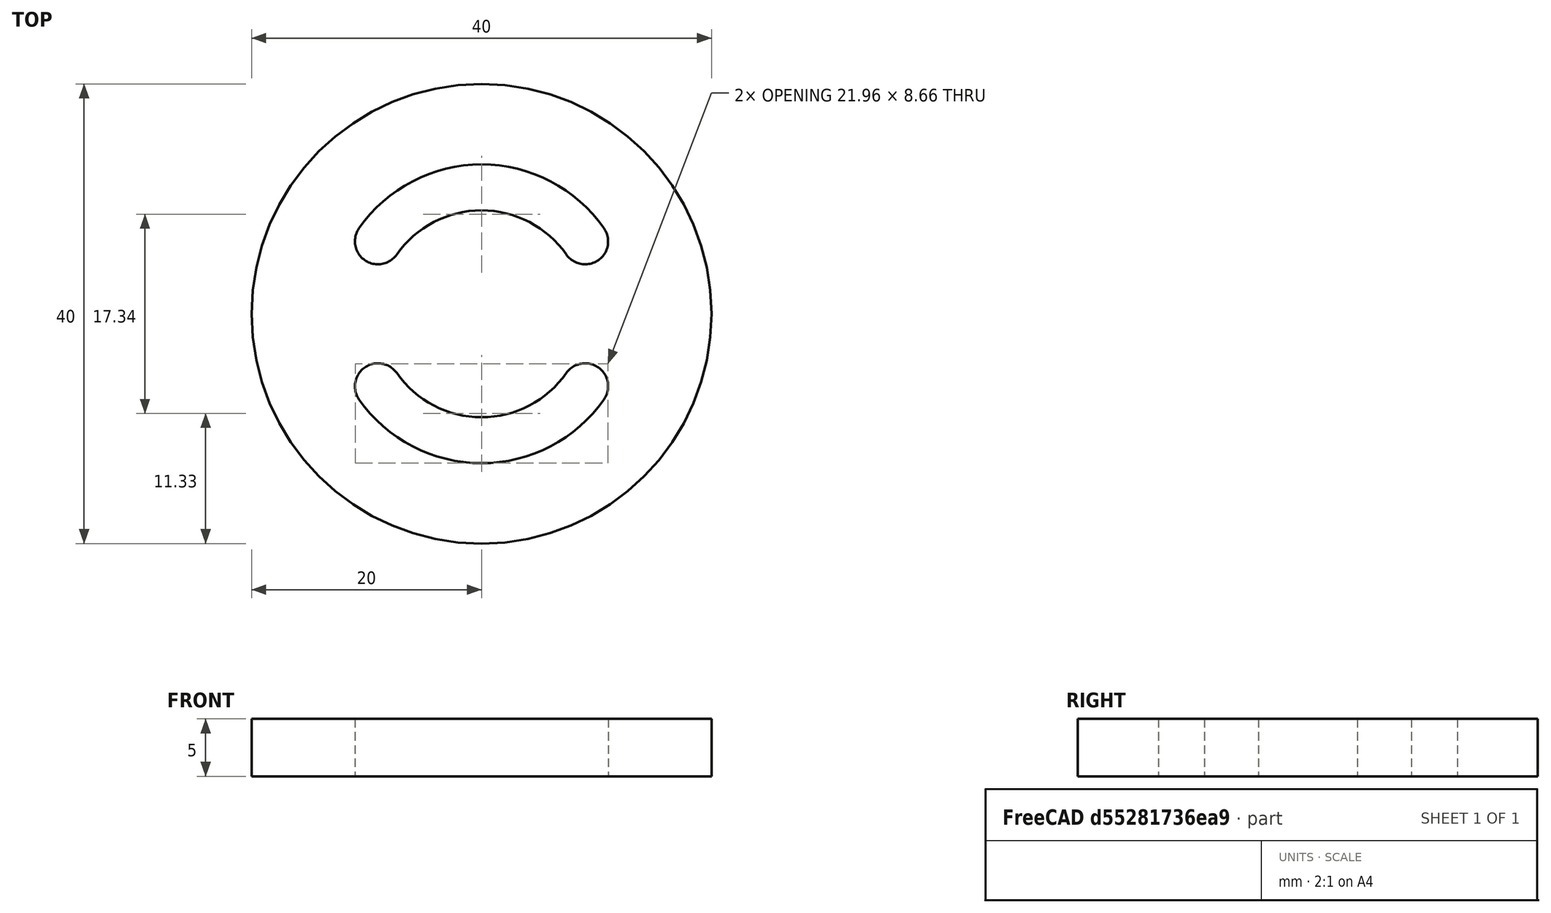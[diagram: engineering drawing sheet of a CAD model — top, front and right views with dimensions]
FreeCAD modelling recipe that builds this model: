
FCSTD DOCUMENT  (FreeCAD 0.16RUnknown)
Label: joint-i
License: All rights reserved
LicenseURL: http://en.wikipedia.org/wiki/All_rights_reserved
objects: Sketcher::SketchObject×1, Part::Extrusion×1
note: 2 computed .brp shape members not serialized (recipe doc carries the construction recipe); baked Part::Feature solids carry a one-line shape summary decoded from their .brp

FEATURE [Sketcher::SketchObject] Sketch
  sketch-geometry (23):
    g0: Circle CenterX=0 CenterY=0 CenterZ=0 NormalX=0 NormalY=0 NormalZ=1 Radius=20
    g1: ArcOfCircle [constr] CenterX=0 CenterY=0 CenterZ=0 NormalX=0 NormalY=0 NormalZ=1 Radius=13 StartAngle=2.53073 EndAngle=3.75246
    g2: ArcOfCircle [constr] CenterX=0 CenterY=0 CenterZ=0 NormalX=0 NormalY=0 NormalZ=1 Radius=9 StartAngle=2.53073 EndAngle=3.75246
    g3: ArcOfCircle [constr] CenterX=0 CenterY=0 CenterZ=0 NormalX=0 NormalY=0 NormalZ=1 Radius=9 StartAngle=5.67232 EndAngle=6.89405
    g4: ArcOfCircle [constr] CenterX=0 CenterY=0 CenterZ=0 NormalX=0 NormalY=0 NormalZ=1 Radius=13 StartAngle=5.67232 EndAngle=6.89405
    g5: ArcOfCircle CenterX=0 CenterY=0 CenterZ=0 NormalX=0 NormalY=0 NormalZ=1 Radius=9 StartAngle=0.610865 EndAngle=2.53073
    g6: ArcOfCircle CenterX=0 CenterY=0 CenterZ=0 NormalX=0 NormalY=0 NormalZ=1 Radius=13 StartAngle=0.610865 EndAngle=2.53073
    g7: ArcOfCircle CenterX=0 CenterY=0 CenterZ=0 NormalX=0 NormalY=0 NormalZ=1 Radius=9 StartAngle=3.75246 EndAngle=5.67232
    g8: ArcOfCircle CenterX=0 CenterY=0 CenterZ=0 NormalX=0 NormalY=0 NormalZ=1 Radius=13 StartAngle=3.75246 EndAngle=5.67232
    g9: LineSegment [constr] StartX=-10.649 StartY=7.45649 StartZ=0 EndX=-7.37237 EndY=5.16219 EndZ=0
    g10: LineSegment [constr] StartX=-7.37237 StartY=5.16219 StartZ=0 EndX=0 EndY=0 EndZ=0
    g11: LineSegment [constr] StartX=0 StartY=0 StartZ=0 EndX=7.37237 EndY=-5.16219 EndZ=0
    g12: LineSegment [constr] StartX=7.37237 StartY=-5.16219 StartZ=0 EndX=10.649 EndY=-7.45649 EndZ=0
    g13: LineSegment [constr] StartX=10.649 StartY=7.45649 StartZ=0 EndX=7.37237 EndY=5.16219 EndZ=0
    g14: LineSegment [constr] StartX=7.37237 StartY=5.16219 StartZ=0 EndX=0 EndY=0 EndZ=0
    g15: LineSegment [constr] StartX=0 StartY=0 StartZ=0 EndX=-7.37237 EndY=-5.16219 EndZ=0
    g16: LineSegment [constr] StartX=-7.37237 StartY=-5.16219 StartZ=0 EndX=-10.649 EndY=-7.45649 EndZ=0
    g17: ArcOfCircle CenterX=-9.01067 CenterY=6.30934 CenterZ=0 NormalX=0 NormalY=0 NormalZ=1 Radius=2 StartAngle=2.53073 EndAngle=5.67232
    g18: ArcOfCircle CenterX=-9.01067 CenterY=-6.30934 CenterZ=0 NormalX=0 NormalY=0 NormalZ=1 Radius=2 StartAngle=0.610865 EndAngle=3.75246
    g19: ArcOfCircle CenterX=9.01067 CenterY=-6.30934 CenterZ=0 NormalX=0 NormalY=0 NormalZ=1 Radius=2 StartAngle=5.67232 EndAngle=8.81391
    g20: ArcOfCircle CenterX=9.01067 CenterY=6.30934 CenterZ=0 NormalX=0 NormalY=0 NormalZ=1 Radius=2 StartAngle=3.75246 EndAngle=6.89405
    g21: LineSegment [constr] StartX=-7.37237 StartY=-5.16219 StartZ=0 EndX=7.37237 EndY=-5.16219 EndZ=0
    g22: LineSegment [constr] StartX=10.649 StartY=7.45649 StartZ=0 EndX=16.383 EndY=11.4715 EndZ=0
  constraints (61):
    c: Coincident(g0,g1)
    c: Coincident(g0,g2)
    c: Coincident(g0,g3)
    c: Coincident(g0,g4)
    c: Coincident(g0,g5)
    c: Coincident(g0,g6)
    c: Coincident(g0,g7)
    c: Coincident(g0,g8)
    c: Coincident(g0,g-1)
    c: Coincident(g4,g6)
    c: Coincident(g4,g8)
    c: Coincident(g1,g8)
    c: Coincident(g2,g7)
    c: Coincident(g2,g5)
    c: Coincident(g1,g6)
    c: Coincident(g3,g5)
    c: Coincident(g3,g7)
    c: Coincident(g9,g10)
    c: Coincident(g10,g11)
    c: Coincident(g11,g12)
    c: Coincident(g1,g9)
    c: Coincident(g2,g9)
    c: Coincident(g0,g10)
    c: Coincident(g3,g11)
    c: Coincident(g4,g12)
    c: Parallel(g9,g10)
    c: Parallel(g10,g11)
    c: Parallel(g11,g12)
    c: Coincident(g13,g14)
    c: Coincident(g14,g15)
    c: Coincident(g15,g16)
    c: Coincident(g1,g16)
    c: Coincident(g2,g15)
    c: Coincident(g0,g14)
    c: Coincident(g3,g13)
    c: Coincident(g4,g13)
    c: Parallel(g13,g14)
    c: Parallel(g14,g15)
    c: Parallel(g15,g16)
    c: Coincident(g4,g20)
    c: Coincident(g3,g20)
    c: Coincident(g2,g17)
    c: Coincident(g1,g17)
    c: Coincident(g2,g18)
    c: Coincident(g1,g18)
    c: Coincident(g3,g19)
    c: Coincident(g4,g19)
    c: PointOnObject(g19,g12)
    c: PointOnObject(g20,g13)
    c: PointOnObject(g17,g9)
    c: PointOnObject(g18,g16)
    c: Angle(g14,g10) = 1.91986
    c: Distance(g9) = 4
    c: Horizontal(g21)
    c: Coincident(g3,g21)
    c: Coincident(g21,g2)
    c: Coincident(g4,g22)
    c: Parallel(g22,g13)
    c: PointOnObject(g22,g0)
    c: Distance(g22) = 7
    c: Radius(g0) = 20
FEATURE [Part::Extrusion] Extrude
  Base = -> Sketch
  Dir = (0,0,5)
  Solid = true
